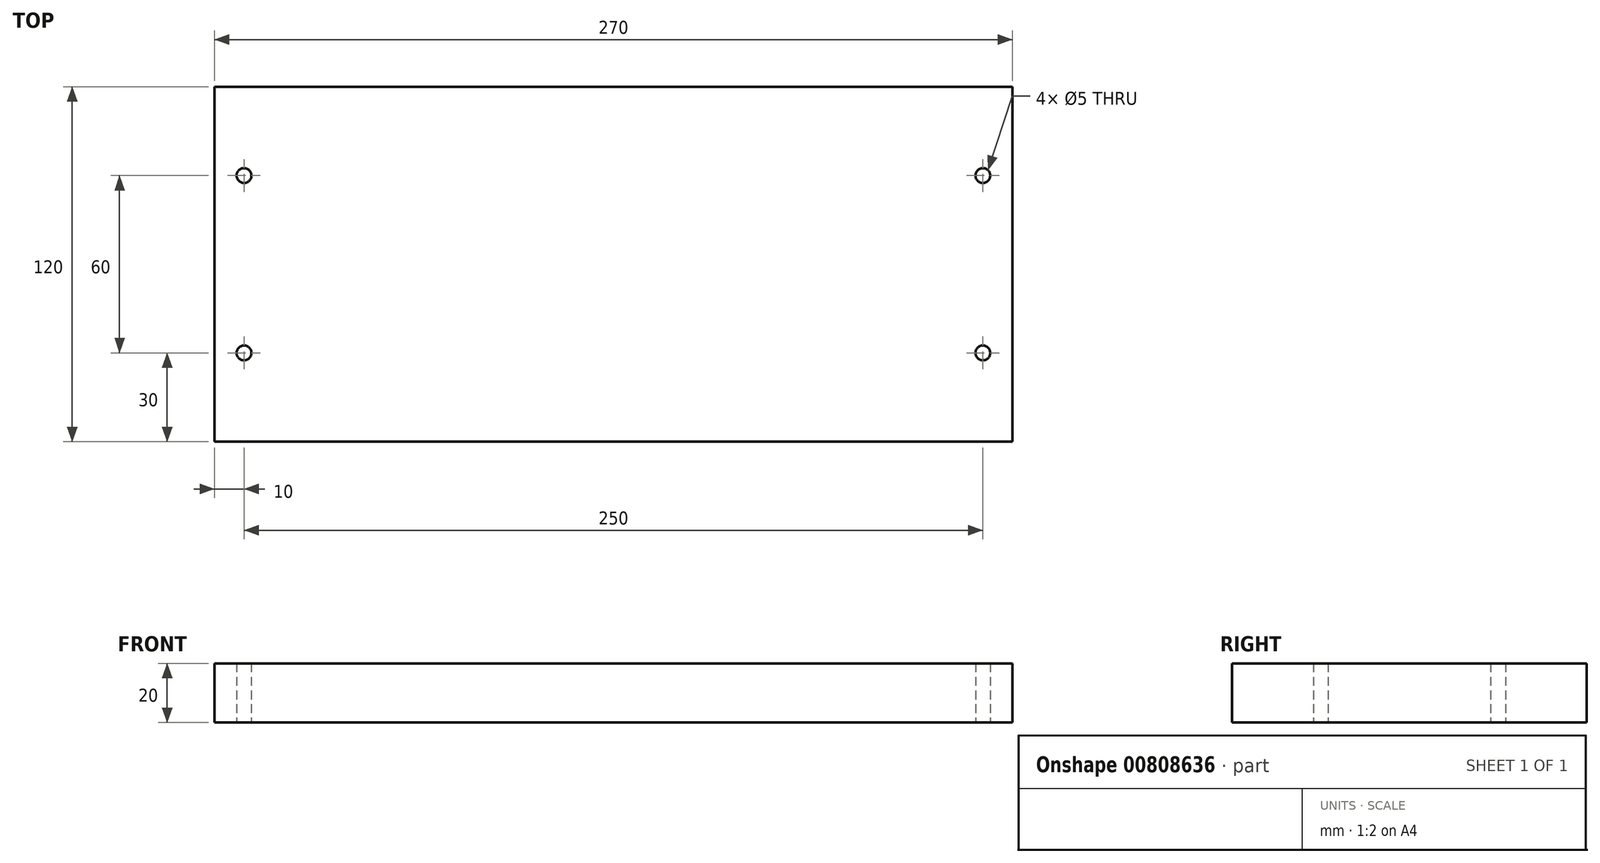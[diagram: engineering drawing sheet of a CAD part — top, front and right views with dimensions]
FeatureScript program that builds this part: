
annotation { "Feature Type Name" : "Feature", "Feature Type Description" : "" }
export const myFeature = defineFeature(function(context is Context, id is Id, definition is map)
    precondition{}
    {
        {
            var Q0;
            Q0=qCreatedBy(makeId("Top.planeOp"),FACE);
            var sketch = newSketch(context, id + "F0", { "sketchPlane" : qUnion([Q0])});
            skLineSegment(sketch, "E0.bottom", {"start": v(-135, 60) * mm, "end": v(135, 60) * mm});
            skLineSegment(sketch, "E0.top", {"start": v(-135, -60) * mm, "end": v(135, -60) * mm});
            skLineSegment(sketch, "E0.left", {"start": v(-135, 60) * mm, "end": v(-135, -60) * mm});
            skLineSegment(sketch, "E0.right", {"start": v(135, 60) * mm, "end": v(135, -60) * mm});
            skPoint(sketch, "E0.middle", {"position": v(0, 0) * mm});
            skLineSegment(sketch, "E1", {"start": v(-135, 60) * mm, "end": v(-125, 60) * mm, "construction": true});
            skLineSegment(sketch, "E2", {"start": v(-125, 60) * mm, "end": v(-125, 30) * mm, "construction": true});
            skLineSegment(sketch, "E3", {"start": v(-125, 30) * mm, "end": v(-125, -30) * mm, "construction": true});
            skCircle(sketch, "E4", {"center": v(-125, 30) * mm, "radius": 2.5 * mm});
            skCircle(sketch, "E5", {"center": v(-125, -30) * mm, "radius": 2.5 * mm});
            skLineSegment(sketch, "E6", {"start": v(135, 60) * mm, "end": v(125, 60) * mm, "construction": true});
            skLineSegment(sketch, "E7", {"start": v(125, 60) * mm, "end": v(125, 30) * mm, "construction": true});
            skLineSegment(sketch, "E8", {"start": v(125, 30) * mm, "end": v(125, -30) * mm, "construction": true});
            skCircle(sketch, "E9", {"center": v(125, 30) * mm, "radius": 2.5 * mm});
            skCircle(sketch, "E10", {"center": v(125, -30) * mm, "radius": 2.5 * mm});
            skSolve(sketch);
        }
        {
            var Q0;
            Q0=makeQuery(id+"F0.imprint","IMPRINT",FACE,{"disambiguationData":[TD([[makeQuery(id+"F0.imprint","IMPRINT",EDGE,{"derivedFrom":sQuery(id+"F0.wireOp",EDGE,"E0.bottom")}),-1.0]])]});
            extrude(context, id + "F1", {"entities" : qUnion([Q0]), "depth" : 20 * mm, "offsetDistance" : 25 * mm});
        }
    });
